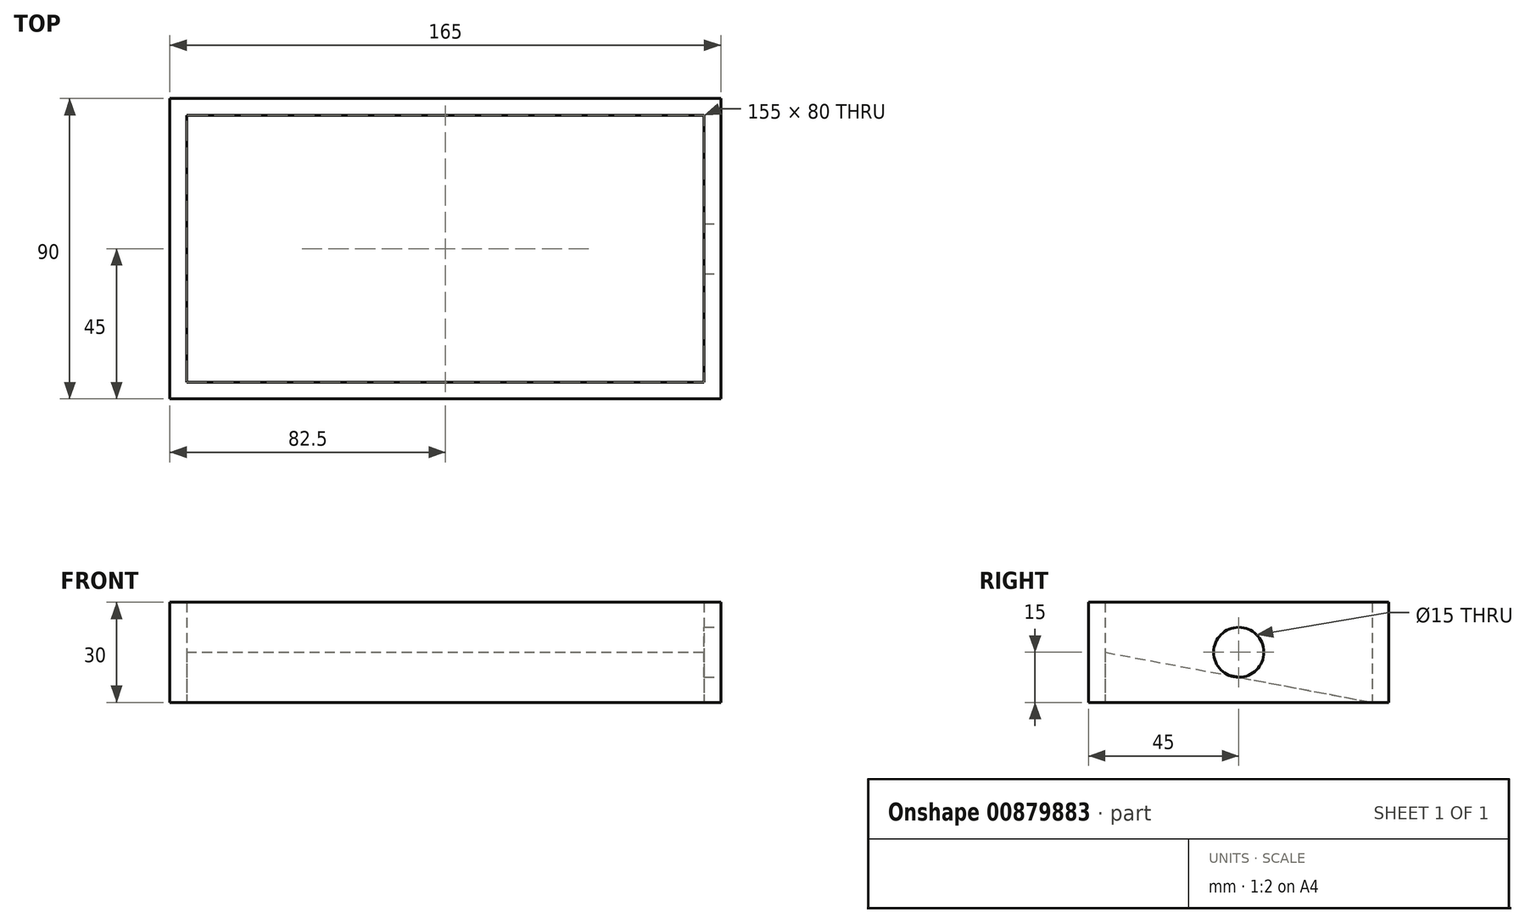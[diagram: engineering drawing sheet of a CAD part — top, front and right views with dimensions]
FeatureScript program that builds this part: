
annotation { "Feature Type Name" : "Feature", "Feature Type Description" : "" }
export const myFeature = defineFeature(function(context is Context, id is Id, definition is map)
    precondition{}
    {
        {
            var Q0;
            Q0=qCreatedBy(makeId("Top.planeOp"),FACE);
            var sketch = newSketch(context, id + "F0", { "sketchPlane" : qUnion([Q0])});
            skLineSegment(sketch, "E0.bottom", {"start": v(0, 0) * mm, "end": v(165, 0) * mm});
            skLineSegment(sketch, "E0.top", {"start": v(0, 90) * mm, "end": v(165, 90) * mm});
            skLineSegment(sketch, "E0.left", {"start": v(0, 0) * mm, "end": v(0, 90) * mm});
            skLineSegment(sketch, "E0.right", {"start": v(165, 0) * mm, "end": v(165, 90) * mm});
            skLineSegment(sketch, "E1.0", {"start": v(5, 85) * mm, "end": v(160, 85) * mm});
            skLineSegment(sketch, "E1.1", {"start": v(5, 5) * mm, "end": v(5, 85) * mm});
            skLineSegment(sketch, "E1.2", {"start": v(5, 5) * mm, "end": v(160, 5) * mm});
            skLineSegment(sketch, "E1.3", {"start": v(160, 5) * mm, "end": v(160, 85) * mm});
            skSolve(sketch);
        }
        {
            var Q0;
            Q0=makeQuery(id+"F0.imprint","IMPRINT",FACE,{"disambiguationData":[TD([[makeQuery(id+"F0.imprint","IMPRINT",EDGE,{"derivedFrom":sQuery(id+"F0.wireOp",EDGE,"E1.0")}),-1.0]])]});
            extrude(context, id + "F1", {"entities" : qUnion([Q0]), "depth" : 15 * mm, "offsetDistance" : 25 * mm});
        }
        {
            var Q0;
            Q0=makeQuery(id+"F1.opExtrude","SWEPT_FACE",FACE,{"disambiguationData":[OSD([sQuery(id+"F0.wireOp",EDGE,"E1.3")])]});
            var sketch = newSketch(context, id + "F2", { "sketchPlane" : qUnion([Q0])});
            skLineSegment(sketch, "E2", {"start": v(5, 15) * mm, "end": v(85, 0) * mm});
            skSolve(sketch);
        }
        {
            var Q0;
            Q0=makeQuery(id+"F2.imprint","IMPRINT",FACE,{"disambiguationData":[TD([[makeQuery(id+"F2.imprint","IMPRINT",EDGE,{"derivedFrom":sQuery(id+"F2.wireOp",EDGE,"E2")}),1.0]])]});
            extrude(context, id + "F3", {"entities" : qUnion([Q0]), "operationType" : NewBodyOperationType.REMOVE, "oppositeDirection" : true, "depth" : 155 * mm, "offsetDistance" : 25 * mm});
        }
        {
            var Q0;
            Q0=makeQuery(id+"F0.imprint","IMPRINT",FACE,{"disambiguationData":[TD([[makeQuery(id+"F0.imprint","IMPRINT",EDGE,{"derivedFrom":sQuery(id+"F0.wireOp",EDGE,"E0.bottom")}),1.0]])]});
            extrude(context, id + "F4", {"entities" : qUnion([Q0]), "depth" : 30 * mm, "offsetDistance" : 25 * mm});
        }
        {
            var Q0;
            Q0=makeQuery(id+"F4.opExtrude","SWEPT_FACE",FACE,{"disambiguationData":[OSD([sQuery(id+"F0.wireOp",EDGE,"E0.right")])]});
            var sketch = newSketch(context, id + "F5", { "sketchPlane" : qUnion([Q0])});
            skCircle(sketch, "E3", {"center": v(45, 15) * mm, "radius": 7.5 * mm});
            skPoint(sketch, "E3.centerSnap0", {"position": v(0, 15) * mm});
            skPoint(sketch, "E3.centerSnap1", {"position": v(45, 30) * mm});
            skSolve(sketch);
        }
        {
            var Q0;
            Q0 = qSketchRegion(id + "F5", true);
            extrude(context, id + "F6", {"entities" : qUnion([Q0]), "operationType" : NewBodyOperationType.REMOVE, "oppositeDirection" : true, "depth" : 5 * mm, "offsetDistance" : 25 * mm});
        }
    });
